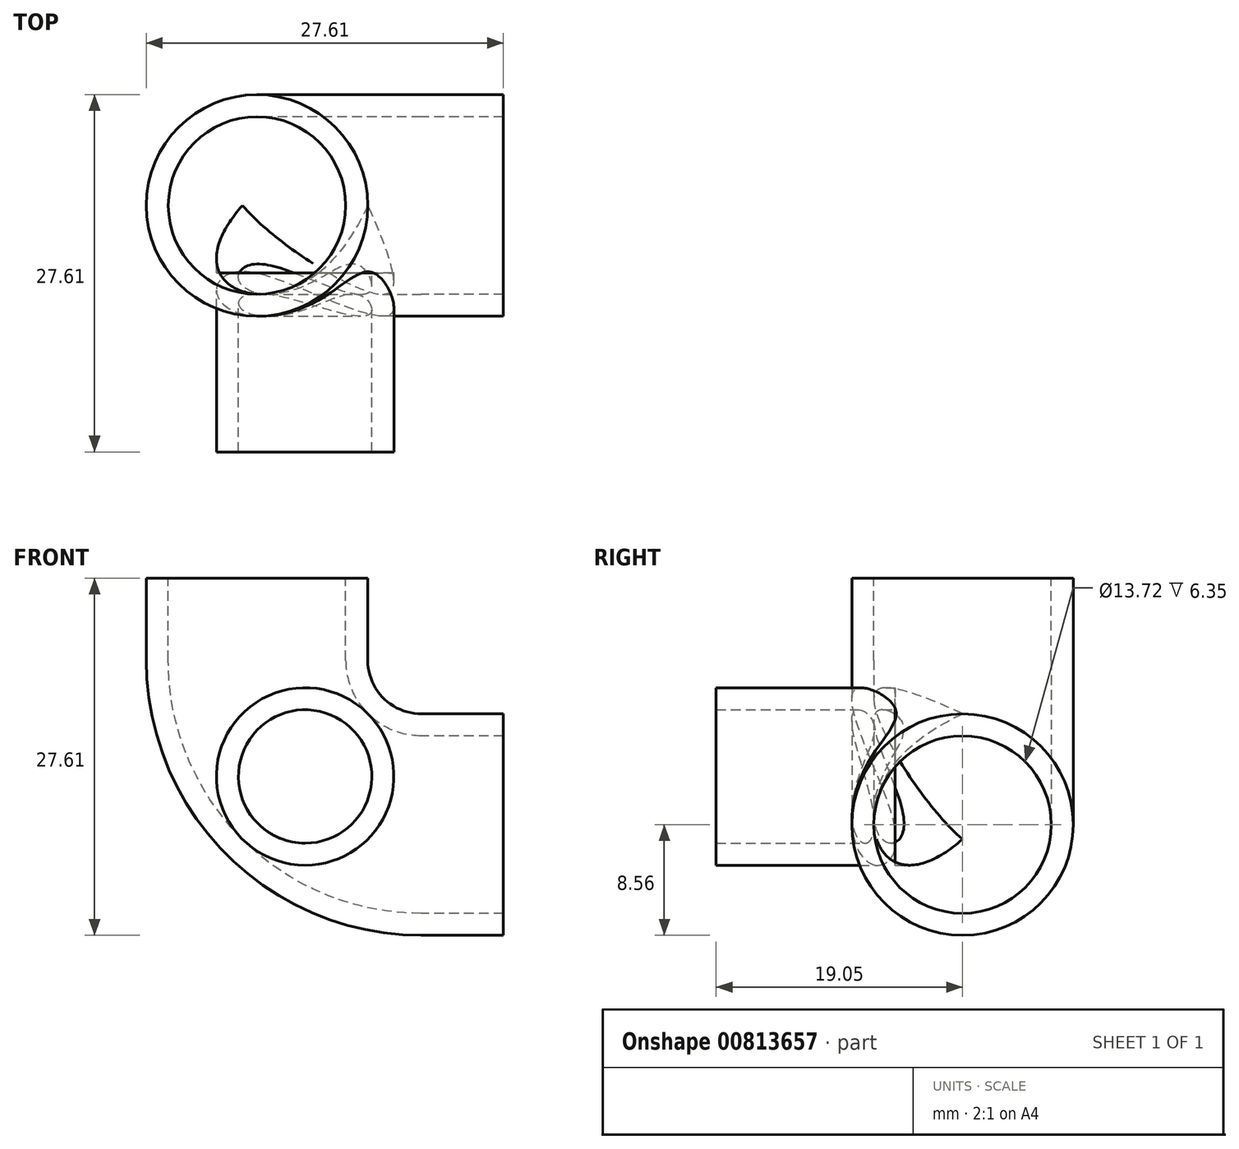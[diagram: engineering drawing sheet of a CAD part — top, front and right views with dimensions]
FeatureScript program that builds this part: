
annotation { "Feature Type Name" : "Feature", "Feature Type Description" : "" }
export const myFeature = defineFeature(function(context is Context, id is Id, definition is map)
    precondition{}
    {
        {
            var Q0;
            Q0=qCreatedBy(makeId("Front.planeOp"),FACE);
            var sketch = newSketch(context, id + "F0", { "sketchPlane" : qUnion([Q0])});
            skLineSegment(sketch, "E0", {"start": v(0, 0) * mm, "end": v(-6.35, 0) * mm});
            skLineSegment(sketch, "E1", {"start": v(-19.05, 12.7) * mm, "end": v(-19.05, 19.05) * mm});
            skPoint(sketch, "E2.visualSharp", {"position": v(-19.05, 0) * mm});
            skArc(sketch, "E2.filletArc", {"start": v(-19.05, 12.7) * mm, "mid": v(-15.33, 3.72) * mm, "end": v(-6.35, 0) * mm});
            skSolve(sketch);
        }
        {
            var Q0;
            Q0=qCreatedBy(makeId("Right.planeOp"),FACE);
            var sketch = newSketch(context, id + "F1", { "sketchPlane" : qUnion([Q0])});
            skCircle(sketch, "E3", {"center": v(0, 0) * mm, "radius": 8.56 * mm});
            skCircle(sketch, "E4", {"center": v(0, 0) * mm, "radius": 6.86 * mm});
            skSolve(sketch);
        }
        {
            var Q0;
            Q0 = qSketchRegion(id + "F1", true);
            var Q1;
            Q1 = qConstructionFilter(qBodyType(qCreatedBy(id + "F0" ,EDGE), BodyType.WIRE), ConstructionObject.NO);
            sweep(context, id + "F2", {"profiles" : qUnion([Q0]), "path" : qUnion([Q1])});
        }
        {
            var Q0;
            Q0=qCreatedBy(makeId("Front.planeOp"),FACE);
            var sketch = newSketch(context, id + "F3", { "sketchPlane" : qUnion([Q0])});
            skLineSegment(sketch, "E5", {"start": v(0, 0) * mm, "end": v(-6.35, 0) * mm});
            skLineSegment(sketch, "E6", {"start": v(-19.05, 12.7) * mm, "end": v(-19.05, 19.05) * mm});
            skPoint(sketch, "E7.visualSharp", {"position": v(-19.05, 0) * mm});
            skArc(sketch, "E7.filletArc", {"start": v(-19.05, 12.7) * mm, "mid": v(-15.33, 3.72) * mm, "end": v(-6.35, 0) * mm});
            skPoint(sketch, "E8", {"position": v(-15.33, 3.72) * mm});
            skCircle(sketch, "E9", {"center": v(-15.33, 3.72) * mm, "radius": 6.86 * mm});
            skCircle(sketch, "E10", {"center": v(-15.33, 3.72) * mm, "radius": 5.16 * mm});
            skSolve(sketch);
        }
        {
            var Q0;
            Q0 = qSketchRegion(id + "F3", true);
            extrude(context, id + "F4", {"entities" : qUnion([Q0]), "operationType" : NewBodyOperationType.ADD, "depth" : 19.05 * mm, "offsetDistance" : 25.4 * mm});
        }
        {
            var Q0;
            Q0 = qSketchRegion(id + "F3", true);
            extrude(context, id + "F5", {"entities" : qUnion([Q0]), "operationType" : NewBodyOperationType.REMOVE, "depth" : 5.2 * mm, "offsetDistance" : 25.4 * mm});
        }
    });
